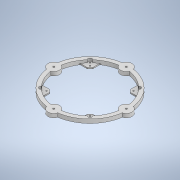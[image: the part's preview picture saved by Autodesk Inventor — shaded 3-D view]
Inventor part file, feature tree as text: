
AUTODESK INVENTOR PART (.ipt)
format: ipt  version: 2022 (Build 260153000, 153)  size: 260,096 bytes
history: native  units: mm
features: sketch x7, extrude x6, fillet x1, pattern_circular x1
ambient origin geometry x8: Origin, YZ Plane, XZ Plane, XY Plane, X Axis, Y Axis, Z Axis, Center Point
bodies: Solid1 (feature_tree)
feature tree (15):
  extrude  "Extrusion1"  Depth=10.0mm TaperAngle=0.0deg
  extrude  "Extrusion13"  Depth=20.0mm TaperAngle=0.0deg
  extrude  "Extrusion16"  Depth=25.0mm
  extrude  "Extrusion17"  TaperAngle=135.0deg  [1 undecoded]
  extrude  "Extrusion18"  Depth=3.5mm
  fillet  "Fillet1"  Radius=9.5mm
  pattern_circular  "Circular Pattern5"  [2 undecoded]
  extrude  "Extrusion20"  Depth=10.0mm
  sketch  "Sketch1"  dims[d0=200.0mm d1=10.0mm d2=0.0mm]
  sketch  "Sketch15"  dims[d139=180.0mm d140=20.0mm d141=0.0mm]
  sketch  "Sketch19"  dims[d162=45.0deg d164=25.0mm]
  sketch  "Sketch20"  dims[d165=135.0deg d166=135.0deg]
  sketch  "Sketch21"  dims[d167=3.5mm d168=3.5mm d169=9.5mm]
  sketch  "Sketch22"  dims[d170=19.5mm]
  sketch  "Sketch23"  dims[d171=10.0mm d172=0.0mm d174=19.5mm d175=9.5mm d176=3.5mm d177=3.5mm d178=10.0mm d179=0.0mm d180=10.0mm d181=10.0mm d182=7.0mm d183=0.0mm d184=2.0mm d185=40.0mm d186=360.0deg d194=4.4mm d195=95.0mm d196=40.0mm d198=360.0deg d200=10.0mm d201=0.0mm d202=30.0mm d208=10.0mm d209=0.0mm d210=95.0mm d211=30.0mm d212=40.0mm d214=360.0deg]
note: 3 required parameter values undecoded (feature->parameter linkage not recoverable at this tier; creation-order binding heuristic only, values carry confidence <= 0.55)
